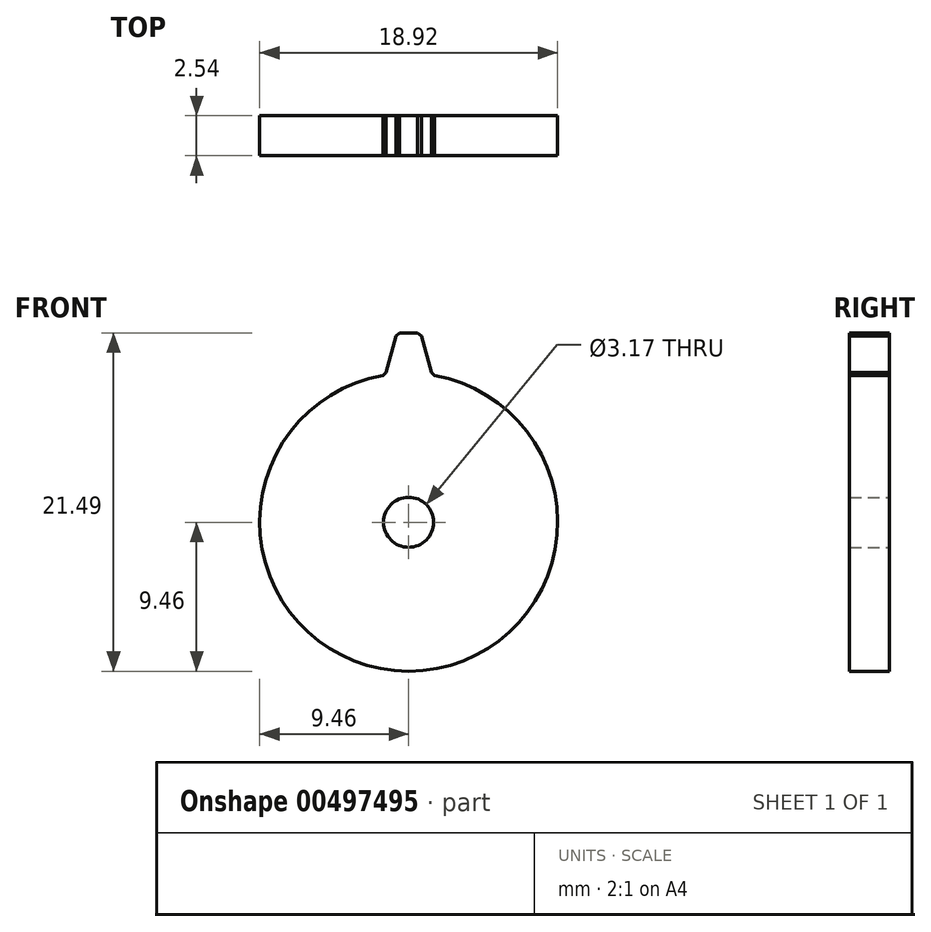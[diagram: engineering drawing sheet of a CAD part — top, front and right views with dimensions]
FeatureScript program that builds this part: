
annotation { "Feature Type Name" : "Feature", "Feature Type Description" : "" }
export const myFeature = defineFeature(function(context is Context, id is Id, definition is map)
    precondition{}
    {
        {
            var Q0;
            Q0=qCreatedBy(makeId("Front.planeOp"),FACE);
            var sketch = newSketch(context, id + "F0", { "sketchPlane" : qUnion([Q0])});
            skCircle(sketch, "E0", {"center": v(0, 0) * mm, "radius": 10.8 * mm, "construction": true});
            skCircle(sketch, "E1", {"center": v(0, 0) * mm, "radius": 9.46 * mm});
            skSolve(sketch);
        }
        {
            var Q0;
            Q0=makeQuery(id+"F0.imprint","IMPRINT",FACE,{"disambiguationData":[TD([[makeQuery(id+"F0.imprint","IMPRINT",EDGE,{"derivedFrom":sQuery(id+"F0.wireOp",EDGE,"E1")}),1.0]])]});
            var sketch = newSketch(context, id + "F1", { "sketchPlane" : qUnion([Q0])});
            skCircle(sketch, "E2", {"center": v(0, 0) * mm, "radius": 1.59 * mm});
            skSolve(sketch);
        }
        {
            var Q0;
            Q0=makeQuery(id+"F0.imprint","IMPRINT",FACE,{"disambiguationData":[TD([[makeQuery(id+"F0.imprint","IMPRINT",EDGE,{"derivedFrom":sQuery(id+"F0.wireOp",EDGE,"E1")}),1.0]])]});
            var sketch = newSketch(context, id + "F2", { "sketchPlane" : qUnion([Q0])});
            skLineSegment(sketch, "E3", {"start": v(0, 0) * mm, "end": v(0, 54.72) * mm, "construction": true});
            skLineSegment(sketch, "E4", {"start": v(0, 12.03) * mm, "end": v(0.76, 12.03) * mm});
            skLineSegment(sketch, "E5", {"start": v(0.76, 12.03) * mm, "end": v(1.66, 8.67) * mm});
            skLineSegment(sketch, "E6", {"start": v(-1.66, 8.67) * mm, "end": v(-0.76, 12.03) * mm});
            skLineSegment(sketch, "E7", {"start": v(-0.76, 12.03) * mm, "end": v(0, 12.03) * mm});
            skLineSegment(sketch, "E8", {"start": v(-1.66, 8.67) * mm, "end": v(1.66, 8.67) * mm});
            skSolve(sketch);
        }
        {
            var Q0;
            Q0=qCreatedBy(makeId("Right.planeOp"),FACE);
            var sketch = newSketch(context, id + "F3", { "sketchPlane" : qUnion([Q0])});
            skLineSegment(sketch, "E9", {"start": v(0, 0) * mm, "end": v(-34.34, 0) * mm, "construction": true});
            skSolve(sketch);
        }
        {
            var Q0;
            Q0=qSketchRegion(id+"F0",true);
            extrude(context, id + "F4", {"entities" : qUnion([Q0]), "depth" : 2.54 * mm});
        }
        {
            var Q0;
            Q0=qSketchRegion(id+"F1",true);
            extrude(context, id + "F5", {"entities" : qUnion([Q0]), "operationType" : NewBodyOperationType.REMOVE, "endBound" : BoundingType.THROUGH_ALL, "depth" : 25.4 * mm});
        }
        {
            var Q0;
            Q0=qSketchRegion(id+"F2",true);
            extrude(context, id + "F6", {"entities" : qUnion([Q0]), "operationType" : NewBodyOperationType.ADD, "depth" : 2.54 * mm});
        }
        {
            var Q0;
            Q0=makeQuery(id+"F6.opExtrude","SWEPT_EDGE",EDGE,{"disambiguationData":[OSD([sQuery(id+"F2.wireOp",EDGE,"E4"),sQuery(id+"F2.wireOp",EDGE,"E5")])]});
            var Q1;
            Q1=makeQuery(id+"F6.opExtrude","SWEPT_EDGE",EDGE,{"disambiguationData":[OSD([sQuery(id+"F2.wireOp",EDGE,"E6"),sQuery(id+"F2.wireOp",EDGE,"E7")])]});
            var Q2;
            Q2=makeQuery(id+"F6.boolean.opBoolean","INTERSECT",EDGE,{"derivedFrom":[makeQuery(id+"F4.opExtrude","SWEPT_FACE",FACE,{"disambiguationData":[OSD([sQuery(id+"F0.wireOp",EDGE,"E1")])]}),makeQuery(id+"F6.opExtrude","SWEPT_FACE",FACE,{"disambiguationData":[OSD([sQuery(id+"F2.wireOp",EDGE,"E5")])]})]});
            var Q3;
            Q3=makeQuery(id+"F6.boolean.opBoolean","INTERSECT",EDGE,{"derivedFrom":[makeQuery(id+"F4.opExtrude","SWEPT_FACE",FACE,{"disambiguationData":[OSD([sQuery(id+"F0.wireOp",EDGE,"E1")])]}),makeQuery(id+"F6.opExtrude","SWEPT_FACE",FACE,{"disambiguationData":[OSD([sQuery(id+"F2.wireOp",EDGE,"E6")])]})]});
            chamfer(context, id + "F7", {"entities" : qUnion([Q0, Q1, Q2, Q3]), "width" : 0.25 * mm, "tangentPropagation" : true});
        }
    });
